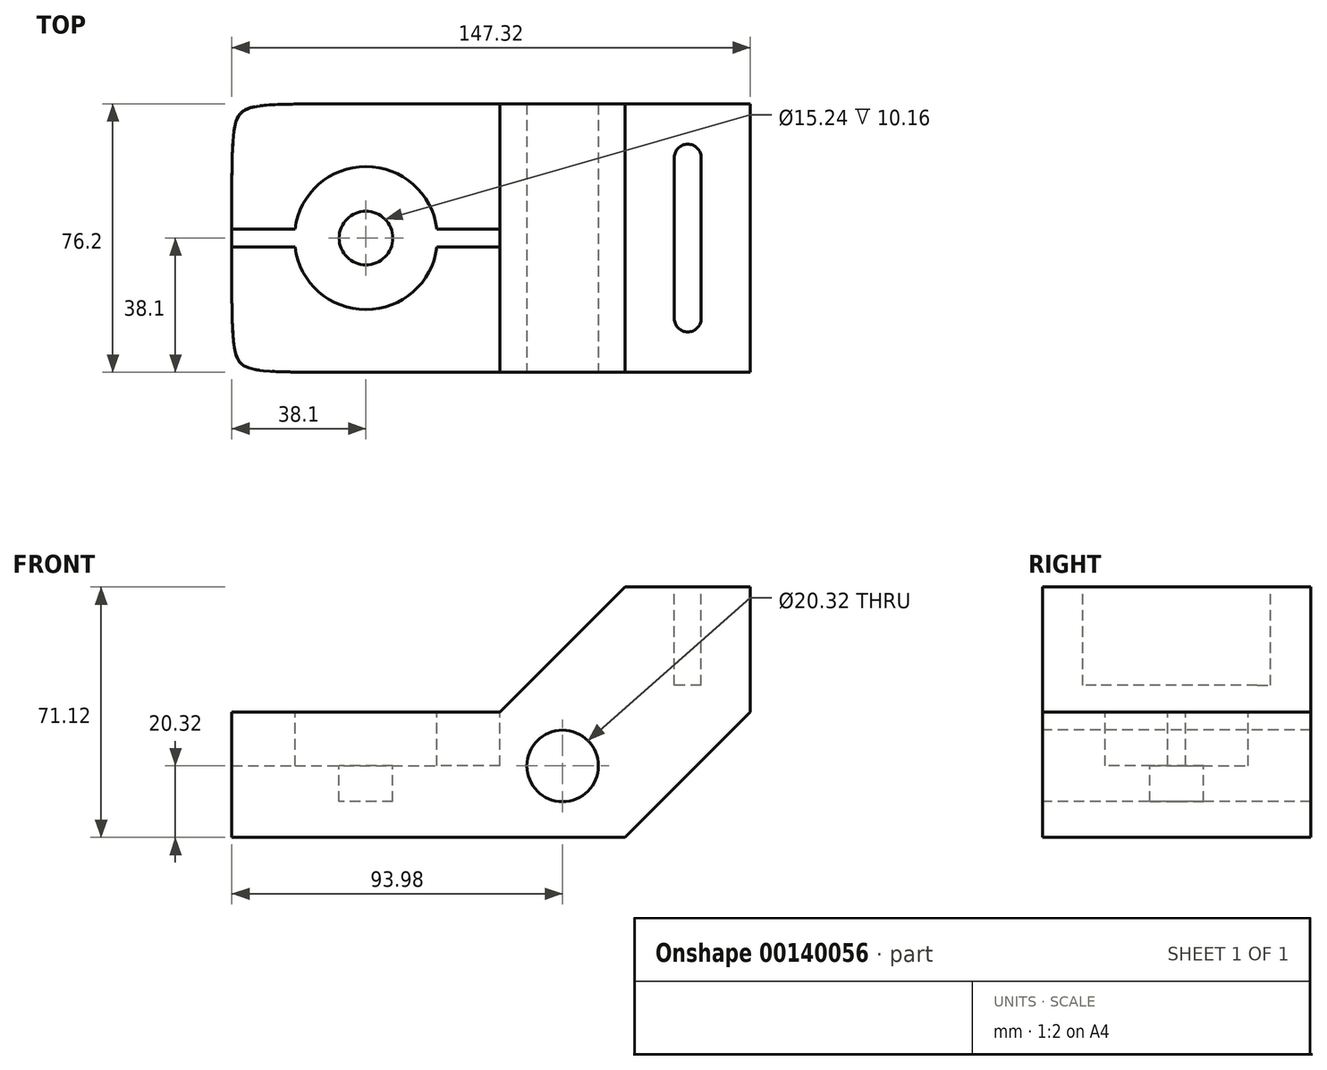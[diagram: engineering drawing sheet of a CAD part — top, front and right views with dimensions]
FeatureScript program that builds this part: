
annotation { "Feature Type Name" : "Feature", "Feature Type Description" : "" }
export const myFeature = defineFeature(function(context is Context, id is Id, definition is map)
    precondition{}
    {
        {
            var Q0;
            Q0=qCreatedBy(makeId("Front.planeOp"),FACE);
            var sketch = newSketch(context, id + "F0", { "sketchPlane" : qUnion([Q0])});
            skLineSegment(sketch, "E0", {"start": v(0, 0) * mm, "end": v(0, 35.56) * mm});
            skLineSegment(sketch, "E1", {"start": v(0, 35.56) * mm, "end": v(76.2, 35.56) * mm});
            skLineSegment(sketch, "E2", {"start": v(0, 0) * mm, "end": v(111.76, 0) * mm});
            skLineSegment(sketch, "E3", {"start": v(111.76, 0) * mm, "end": v(147.32, 35.56) * mm});
            skLineSegment(sketch, "E4", {"start": v(76.2, 35.56) * mm, "end": v(111.76, 71.12) * mm});
            skLineSegment(sketch, "E5", {"start": v(111.76, 71.12) * mm, "end": v(147.32, 71.12) * mm});
            skLineSegment(sketch, "E6", {"start": v(147.32, 71.12) * mm, "end": v(147.32, 35.56) * mm});
            skSolve(sketch);
        }
        {
            var Q0;
            Q0 = qSketchRegion(id + "F0", true);
            extrude(context, id + "F1", {"entities" : qUnion([Q0]), "depth" : 76.2 * mm});
        }
        {
            var Q0;
            Q0=makeQuery(id+"F1.opExtrude","CAP_FACE",FACE,{"disambiguationData":[OSD([sQuery(id+"F0.wireOp",EDGE,"E0"),sQuery(id+"F0.wireOp",EDGE,"E1"),sQuery(id+"F0.wireOp",EDGE,"E2"),sQuery(id+"F0.wireOp",EDGE,"E3"),sQuery(id+"F0.wireOp",EDGE,"E4"),sQuery(id+"F0.wireOp",EDGE,"E5"),sQuery(id+"F0.wireOp",EDGE,"E6")])],"isStart":false});
            var sketch = newSketch(context, id + "F2", { "sketchPlane" : qUnion([Q0])});
            skLineSegment(sketch, "E7", {"start": v(147.32, 20.32) * mm, "end": v(93.98, 20.32) * mm, "construction": true});
            skCircle(sketch, "E8", {"center": v(93.98, 20.32) * mm, "radius": 10.16 * mm});
            skSolve(sketch);
        }
        {
            var Q0;
            Q0 = qSketchRegion(id + "F2", true);
            extrude(context, id + "F3", {"entities" : qUnion([Q0]), "operationType" : NewBodyOperationType.REMOVE, "oppositeDirection" : true, "depth" : 76.2 * mm});
        }
        {
            var Q0;
            Q0=makeQuery(id+"F1.opExtrude","SWEPT_FACE",FACE,{"disambiguationData":[OSD([sQuery(id+"F0.wireOp",EDGE,"E5")])]});
            var sketch = newSketch(context, id + "F4", { "sketchPlane" : qUnion([Q0])});
            skLineSegment(sketch, "E9", {"start": v(129.54, -15.24) * mm, "end": v(129.54, -60.96) * mm, "construction": true});
            skPoint(sketch, "E9.startSnap0", {"position": v(129.54, 0) * mm});
            skArc(sketch, "E10.0.startCap", {"start": v(125.73, -15.24) * mm, "mid": v(129.54, -11.43) * mm, "end": v(133.35, -15.24) * mm});
            skArc(sketch, "E10.0.endCap", {"start": v(133.35, -60.96) * mm, "mid": v(129.54, -64.77) * mm, "end": v(125.73, -60.96) * mm});
            skLineSegment(sketch, "E10.0.left", {"start": v(133.35, -15.24) * mm, "end": v(133.35, -60.96) * mm});
            skLineSegment(sketch, "E10.0.right", {"start": v(125.73, -15.24) * mm, "end": v(125.73, -60.96) * mm});
            skSolve(sketch);
        }
        {
            var Q0;
            Q0 = qSketchRegion(id + "F4", true);
            extrude(context, id + "F5", {"entities" : qUnion([Q0]), "operationType" : NewBodyOperationType.REMOVE, "oppositeDirection" : true, "depth" : 27.94 * mm});
        }
        {
            var Q0;
            Q0=makeQuery(id+"F1.opExtrude","SWEPT_FACE",FACE,{"disambiguationData":[OSD([sQuery(id+"F0.wireOp",EDGE,"E1")])]});
            var sketch = newSketch(context, id + "F6", { "sketchPlane" : qUnion([Q0])});
            skLineSegment(sketch, "E11", {"start": v(76.2, -38.1) * mm, "end": v(0, -38.1) * mm, "construction": true});
            skCircle(sketch, "E12", {"center": v(38.1, -38.1) * mm, "radius": 20.32 * mm});
            skLineSegment(sketch, "E13", {"start": v(76.2, -35.56) * mm, "end": v(58.26, -35.56) * mm});
            skLineSegment(sketch, "E14", {"start": v(76.2, -40.64) * mm, "end": v(58.26, -40.64) * mm});
            skLineSegment(sketch, "E15", {"start": v(0, -35.56) * mm, "end": v(17.94, -35.56) * mm});
            skLineSegment(sketch, "E16", {"start": v(0, -40.64) * mm, "end": v(17.94, -40.64) * mm});
            skLineSegment(sketch, "E17", {"start": v(0, -35.56) * mm, "end": v(0, -40.64) * mm});
            skLineSegment(sketch, "E18", {"start": v(76.2, -35.56) * mm, "end": v(76.2, -40.64) * mm});
            skSolve(sketch);
        }
        {
            var Q0;
            Q0 = qSketchRegion(id + "F6", true);
            extrude(context, id + "F7", {"entities" : qUnion([Q0]), "operationType" : NewBodyOperationType.REMOVE, "oppositeDirection" : true, "depth" : 15.24 * mm});
        }
        {
            var Q0;
            Q0=makeQuery(id+"F7.boolean.opBoolean","COPY",FACE,{"derivedFrom":makeQuery(id+"F7.opExtrude","CAP_FACE",FACE,{"disambiguationData":[OSD([sQuery(id+"F6.wireOp",EDGE,"E12"),sQuery(id+"F6.wireOp",EDGE,"E13"),sQuery(id+"F6.wireOp",EDGE,"E14"),sQuery(id+"F6.wireOp",EDGE,"E15"),sQuery(id+"F6.wireOp",EDGE,"E16"),sQuery(id+"F6.wireOp",EDGE,"E17"),sQuery(id+"F6.wireOp",EDGE,"E18")])],"isStart":false})});
            var sketch = newSketch(context, id + "F8", { "sketchPlane" : qUnion([Q0])});
            skCircle(sketch, "E19", {"center": v(38.1, -38.1) * mm, "radius": 7.62 * mm});
            skSolve(sketch);
        }
        {
            var Q0;
            Q0 = qSketchRegion(id + "F8", true);
            extrude(context, id + "F9", {"entities" : qUnion([Q0]), "operationType" : NewBodyOperationType.REMOVE, "oppositeDirection" : true, "depth" : 10.16 * mm});
        }
        {
            var Q0;
            Q0=makeQuery(id+"F1.opExtrude","CAP_EDGE",EDGE,{"disambiguationData":[OSD([sQuery(id+"F0.wireOp",EDGE,"E0")])],"isStart":false});
            fillet(context, id + "F10", {"entities" : qUnion([Q0]), "radius" : 25.4 * mm, "rho" : .8, "crossSection" : FilletCrossSection.CONIC, "allowEdgeOverflow" : false});
        }
        {
            var Q0;
            Q0=makeQuery(id+"F1.opExtrude","CAP_EDGE",EDGE,{"disambiguationData":[OSD([sQuery(id+"F0.wireOp",EDGE,"E0")])],"isStart":true});
            fillet(context, id + "F11", {"entities" : qUnion([Q0]), "radius" : 25.4 * mm, "tangentPropagation" : true, "rho" : .8, "crossSection" : FilletCrossSection.CONIC, "allowEdgeOverflow" : false});
        }
    });
